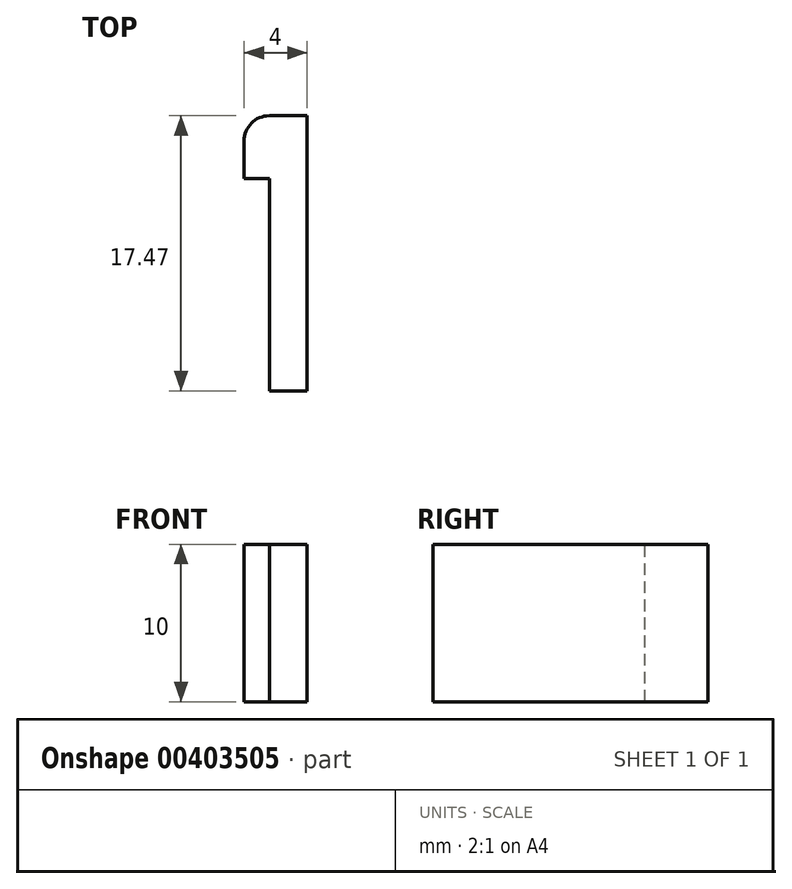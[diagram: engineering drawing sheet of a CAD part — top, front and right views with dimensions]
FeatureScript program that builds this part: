
annotation { "Feature Type Name" : "Feature", "Feature Type Description" : "" }
export const myFeature = defineFeature(function(context is Context, id is Id, definition is map)
    precondition{}
    {
        {
            var Q0;
            Q0=qCreatedBy(makeId("Top.planeOp"),FACE);
            var sketch = newSketch(context, id + "F0", { "sketchPlane" : qUnion([Q0])});
            skLineSegment(sketch, "E0.top", {"start": v(-44.13, 1.21) * mm, "end": v(-41.73, 1.21) * mm});
            skLineSegment(sketch, "E0.left", {"start": v(-44.13, 18.68) * mm, "end": v(-44.13, 1.21) * mm});
            skLineSegment(sketch, "E0.right", {"start": v(-41.73, 18.68) * mm, "end": v(-41.73, 1.21) * mm});
            skLineSegment(sketch, "E1", {"start": v(-44.13, 18.68) * mm, "end": v(-41.73, 18.68) * mm});
            skLineSegment(sketch, "E2.bottom", {"start": v(-44.13, 18.68) * mm, "end": v(-44.13, 18.68) * mm});
            skLineSegment(sketch, "E2.top", {"start": v(-44.13, 14.68) * mm, "end": v(-45.73, 14.68) * mm});
            skLineSegment(sketch, "E2.left", {"start": v(-44.13, 18.68) * mm, "end": v(-44.13, 14.68) * mm});
            skLineSegment(sketch, "E2.right", {"start": v(-45.73, 17.08) * mm, "end": v(-45.73, 14.68) * mm});
            skPoint(sketch, "E3.visualSharp", {"position": v(-45.73, 18.68) * mm});
            skArc(sketch, "E3.filletArc", {"start": v(-44.13, 18.68) * mm, "mid": v(-45.26, 18.21) * mm, "end": v(-45.73, 17.08) * mm});
            skSolve(sketch);
        }
        {
            var Q0;
            Q0=makeQuery(id+"F0.imprint","IMPRINT",FACE,{"disambiguationData":[TD([[makeQuery(id+"F0.imprint","IMPRINT",EDGE,{"derivedFrom":sQuery(id+"F0.wireOp",EDGE,"E0.top")}),1.0]])]});
            var Q1;
            Q1=makeQuery(id+"F0.imprint","IMPRINT",FACE,{"disambiguationData":[TD([[makeQuery(id+"F0.imprint","IMPRINT",EDGE,{"derivedFrom":sQuery(id+"F0.wireOp",EDGE,"E2.top")}),-1.0]])]});
            extrude(context, id + "F1", {"entities" : qUnion([Q0, Q1]), "oppositeDirection" : true, "depth" : 10 * mm});
        }
    });
